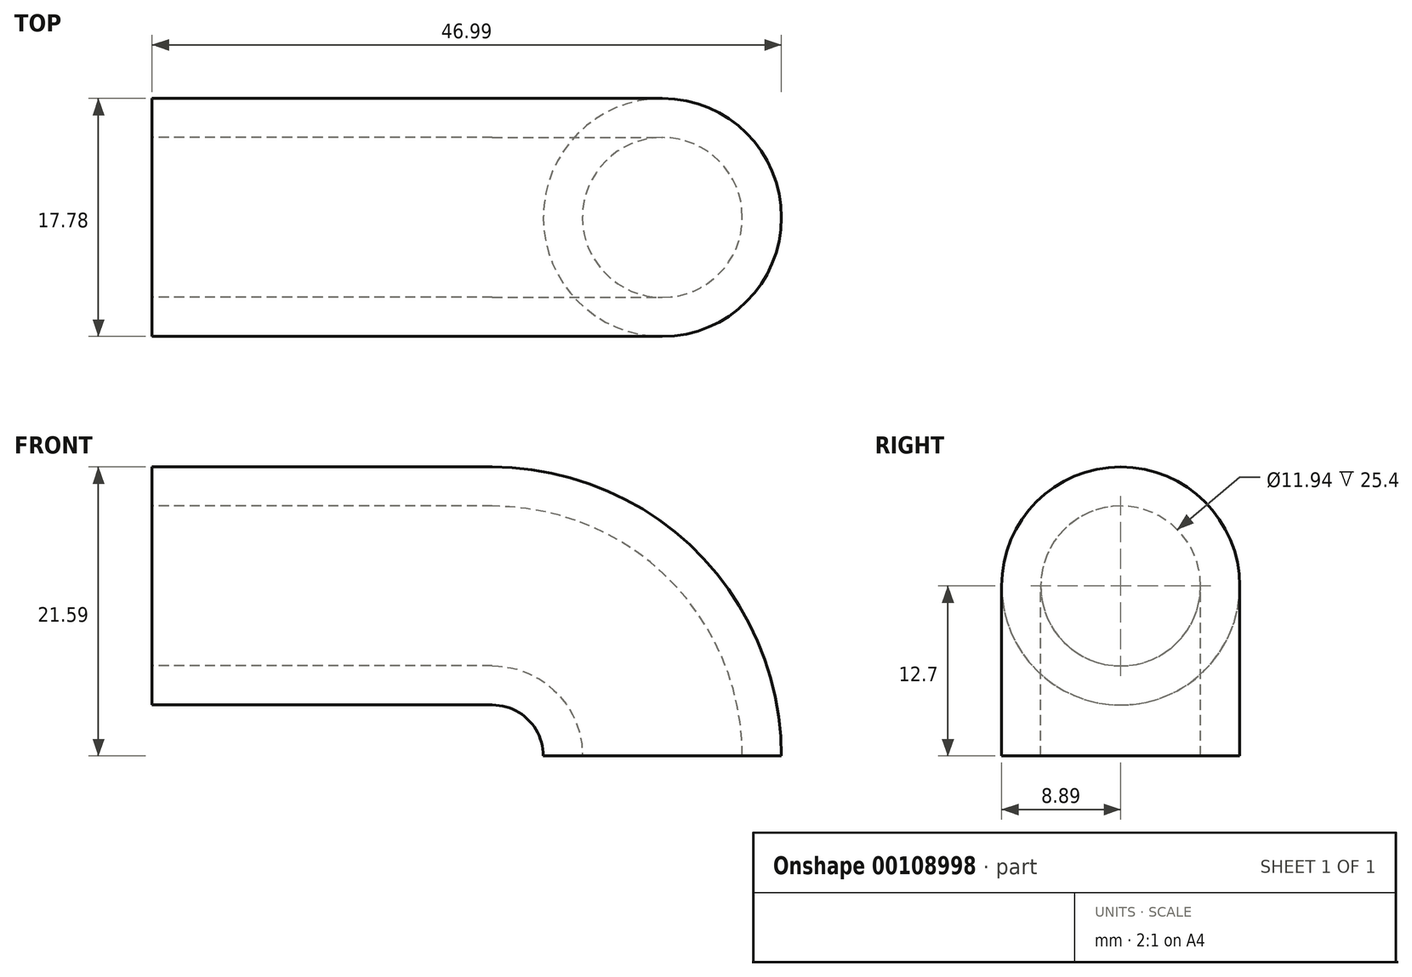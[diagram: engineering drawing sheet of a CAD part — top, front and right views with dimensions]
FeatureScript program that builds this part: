
annotation { "Feature Type Name" : "Feature", "Feature Type Description" : "" }
export const myFeature = defineFeature(function(context is Context, id is Id, definition is map)
    precondition{}
    {
        {
            var Q0;
            Q0=qCreatedBy(makeId("Front.planeOp"),FACE);
            var sketch = newSketch(context, id + "F0", { "sketchPlane" : qUnion([Q0])});
            skLineSegment(sketch, "E0", {"start": v(0, 0) * mm, "end": v(-12.7, 0) * mm});
            skLineSegment(sketch, "E1", {"start": v(0, -23.27) * mm, "end": v(0, -12.7) * mm});
            skArc(sketch, "E2", {"start": v(0, -12.7) * mm, "mid": v(-3.72, -3.72) * mm, "end": v(-12.7, 0) * mm});
            skLineSegment(sketch, "E3", {"start": v(-12.7, 0) * mm, "end": v(-38.1, 0) * mm});
            skSolve(sketch);
        }
        {
            var Q0;
            Q0=sQuery(id+"F0.wireOp",EDGE,"E2");
            var Q1;
            Q1=sQuery(id+"F0.wireOp",VERTEX,"E2.start");
            cPlane(context, id + "F1", {"entities" : qUnion([Q0, Q1]), "cplaneType" : CPlaneType.CURVE_POINT, "offset" : 25.4 * mm, "width" : 152.4 * mm, "height" : 152.4 * mm});
        }
        {
            var Q0;
            Q0=qCreatedBy(id+"F1.planeOp",FACE);
            var sketch = newSketch(context, id + "F2", { "sketchPlane" : qUnion([Q0])});
            skCircle(sketch, "E4", {"center": v(0, 0) * mm, "radius": 5.97 * mm});
            skCircle(sketch, "E5", {"center": v(0, 0) * mm, "radius": 8.9 * mm});
            skSolve(sketch);
        }
        {
            var Q0;
            Q0=makeQuery(id+"F2.imprint","IMPRINT",FACE,{"disambiguationData":[TD([[makeQuery(id+"F2.imprint","IMPRINT",EDGE,{"derivedFrom":sQuery(id+"F2.wireOp",EDGE,"E4")}),-1.0]])]});
            var Q1;
            Q1=sQuery(id+"F0.wireOp",EDGE,"E2");
            var Q2;
            Q2=sQuery(id+"F0.wireOp",EDGE,"E3");
            sweep(context, id + "F3", {"profiles" : qUnion([Q0]), "path" : qUnion([Q1, Q2])});
        }
    });
